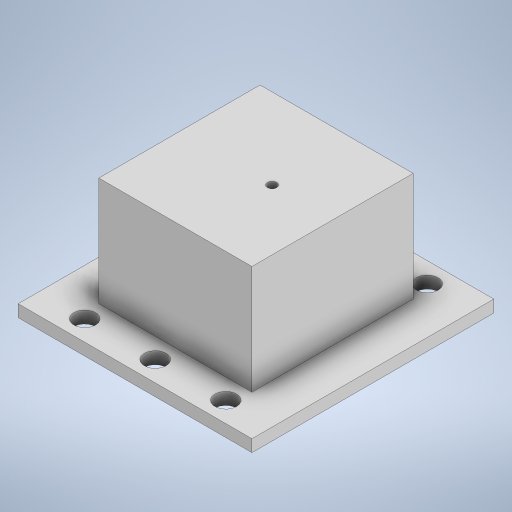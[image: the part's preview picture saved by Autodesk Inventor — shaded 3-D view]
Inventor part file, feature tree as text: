
AUTODESK INVENTOR PART (.ipt)
format: ipt  version: 2024 (Build 280153000, 153)  size: 310,272 bytes
history: native  units: mm
features: extrude x7, sketch x7, plane x3
ambient origin geometry x8: Origin, YZ Plane, XZ Plane, XY Plane, X Axis, Y Axis, Z Axis, Center Point
bodies: Body1 (feature_tree)
feature tree (17):
  plane  "Work Plane5"
  extrude  "Extrusion34"  Depth=40.0mm
  plane  "Work Plane2"
  extrude  "Extrusion35"  Depth=30.0mm
  plane  "Work Plane1"
  extrude  "Extrusion51"  Depth=30.0mm
  sketch  "Sketch77"  dims[d211=10.0mm d212=0.0mm d219=35.0mm]
  extrude  "Extrusion53"  Depth=10.0mm
  extrude  "Extrusion54"  Depth=60.0mm
  extrude  "Extrusion56"  Depth=3.0mm TaperAngle=0.0deg
  extrude  "Extrusion57"  Depth=4.5mm
  sketch  "Sketch45"  dims[d142=38.0mm d143=40.0mm]
  sketch  "Sketch47"  dims[d144=30.0mm d145=0.0mm d146=36.0mm]
  sketch  "Sketch74"  dims[d147=30.0mm d148=-2.617994mm d210=2.3mm]
  sketch  "Sketch78"  dims[d220=58.0mm d221=60.0mm]
  sketch  "Sketch81"  dims[d222=3.0mm d223=0.0mm d224=3.0mm d225=0.0mm]
  sketch  "Sketch83"  dims[d232=5.0mm d233=11.5mm d234=5.4mm d235=17.5mm d236=5.4mm d237=17.5mm d243=5.4mm d245=5.4mm d246=17.5mm d247=5.4mm d248=17.5mm d250=30.0mm d251=0.0mm d253=4.0mm d254=4.5mm d255=0.0mm d49=0.5mm d50=0.872665mm d51=0.5mm d52=0.872665mm d130=0.5mm d131=0.872665mm d132=0.5mm d133=0.872665mm d156=0.5mm d157=0.872665mm d158=0.5mm d159=0.872665mm d173=0.5mm d174=0.872665mm d175=0.5mm d176=0.872665mm d226=0.5mm d227=0.872665mm]
